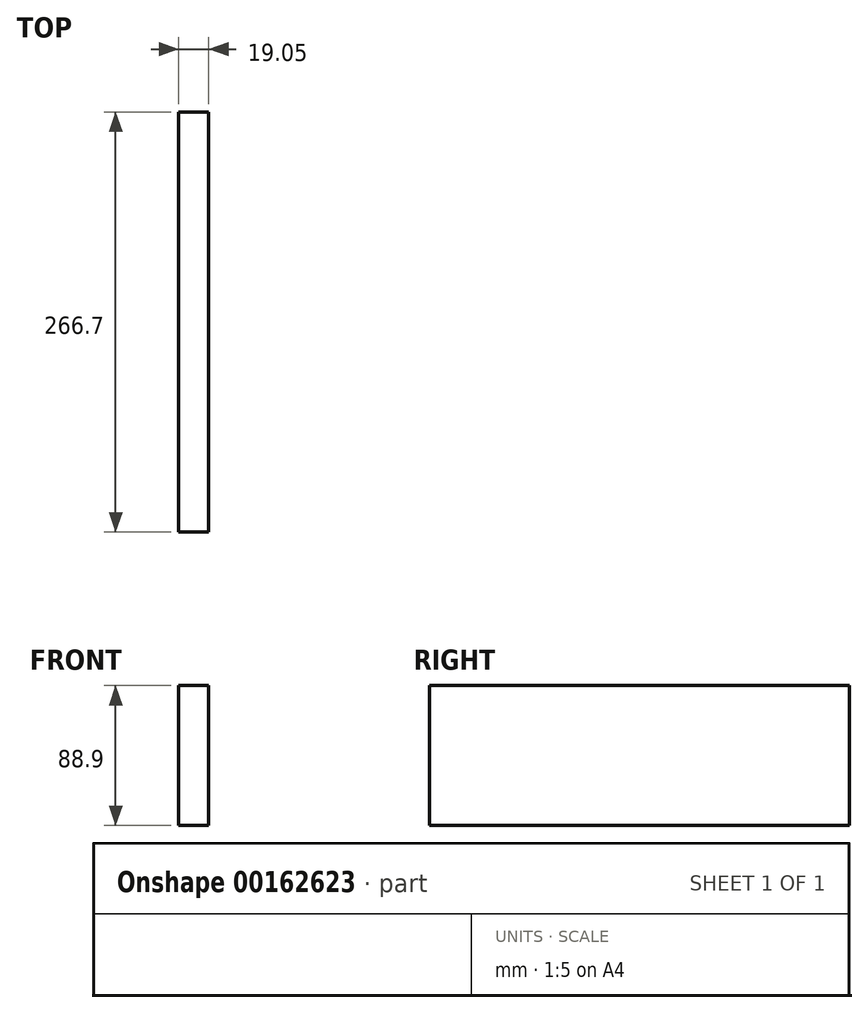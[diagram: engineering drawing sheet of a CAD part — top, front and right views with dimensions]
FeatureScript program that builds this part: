
annotation { "Feature Type Name" : "Feature", "Feature Type Description" : "" }
export const myFeature = defineFeature(function(context is Context, id is Id, definition is map)
    precondition{}
    {
        {
            var Q0;
            Q0=qCreatedBy(makeId("Right.planeOp"),FACE);
            var sketch = newSketch(context, id + "F0", { "sketchPlane" : qUnion([Q0])});
            skLineSegment(sketch, "E0.bottom", {"start": v(-180.63, 66.99) * mm, "end": v(86.07, 66.99) * mm});
            skLineSegment(sketch, "E0.top", {"start": v(-180.63, -21.91) * mm, "end": v(86.07, -21.91) * mm});
            skLineSegment(sketch, "E0.left", {"start": v(-180.63, 66.99) * mm, "end": v(-180.63, -21.91) * mm});
            skLineSegment(sketch, "E0.right", {"start": v(86.07, 66.99) * mm, "end": v(86.07, -21.91) * mm});
            skSolve(sketch);
        }
        {
            var Q0;
            Q0 = qSketchRegion(id + "F0", true);
            extrude(context, id + "F1", {"entities" : qUnion([Q0]), "depth" : 19.05 * mm});
        }
    });
